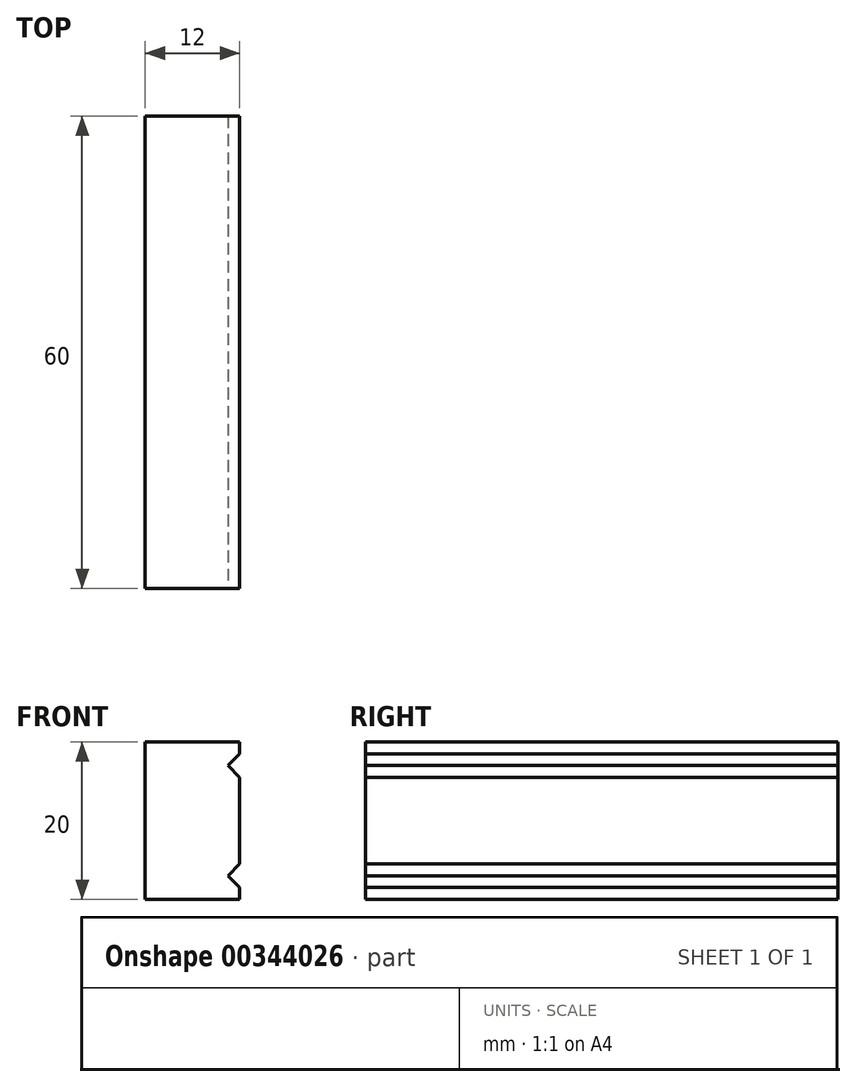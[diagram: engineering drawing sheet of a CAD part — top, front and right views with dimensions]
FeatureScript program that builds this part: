
annotation { "Feature Type Name" : "Feature", "Feature Type Description" : "" }
export const myFeature = defineFeature(function(context is Context, id is Id, definition is map)
    precondition{}
    {
        {
            var Q0;
            Q0=qCreatedBy(makeId("Right.planeOp"),FACE);
            var sketch = newSketch(context, id + "F0", { "sketchPlane" : qUnion([Q0])});
            skLineSegment(sketch, "E0.bottom", {"start": v(30, -10) * mm, "end": v(-30, -10) * mm});
            skLineSegment(sketch, "E0.top", {"start": v(30, 10) * mm, "end": v(-30, 10) * mm});
            skLineSegment(sketch, "E0.left", {"start": v(30, -10) * mm, "end": v(30, 10) * mm});
            skLineSegment(sketch, "E0.right", {"start": v(-30, -10) * mm, "end": v(-30, 10) * mm});
            skPoint(sketch, "E0.middle", {"position": v(0, 0) * mm});
            skSolve(sketch);
        }
        {
            var Q0;
            Q0=makeQuery(id+"F0.imprint","IMPRINT",FACE,{"disambiguationData":[TD([[makeQuery(id+"F0.imprint","IMPRINT",EDGE,{"derivedFrom":sQuery(id+"F0.wireOp",EDGE,"E0.bottom")}),-1.0]])]});
            extrude(context, id + "F1", {"entities" : qUnion([Q0]), "depth" : 12 * mm});
        }
        {
            var Q0;
            Q0=makeQuery(id+"F1.opExtrude","SWEPT_FACE",FACE,{"disambiguationData":[OSD([sQuery(id+"F0.wireOp",EDGE,"E0.right")])]});
            var sketch = newSketch(context, id + "F2", { "sketchPlane" : qUnion([Q0])});
            skLineSegment(sketch, "E1", {"start": v(10.5, 7) * mm, "end": v(12.79, 9.29) * mm});
            skLineSegment(sketch, "E2", {"start": v(10.5, 7) * mm, "end": v(13.4, 4.1) * mm});
            skLineSegment(sketch, "E3", {"start": v(10.5, -7) * mm, "end": v(13.13, -4.37) * mm});
            skLineSegment(sketch, "E4", {"start": v(10.5, -7) * mm, "end": v(16.17, -12.67) * mm});
            skSolve(sketch);
        }
        {
            var Q0;
            {var subQ0=sQuery(id+"F2.wireOp",EDGE,"E2");var subQ1=sQuery(id+"F2.wireOp",EDGE,"E1");var subQ2=makeQuery(id+"F2.imprint","INTERSECT",VERTEX,{"derivedFrom":[subQ1,subQ0]});Q0=makeQuery(id+"F2.imprint","IMPRINT",FACE,{"disambiguationData":[TD([[makeQuery(id+"F2.imprint","IMPRINT",EDGE,{"disambiguationData":[TD([[subQ2,-1.0]])],"derivedFrom":subQ1}),-1.0]])]});}
            var Q1;
            {var subQ0=sQuery(id+"F2.wireOp",EDGE,"E4");var subQ1=sQuery(id+"F2.wireOp",EDGE,"E3");var subQ2=makeQuery(id+"F2.imprint","INTERSECT",VERTEX,{"derivedFrom":[subQ1,subQ0]});Q1=makeQuery(id+"F2.imprint","IMPRINT",FACE,{"disambiguationData":[TD([[makeQuery(id+"F2.imprint","IMPRINT",EDGE,{"disambiguationData":[TD([[subQ2,-1.0]])],"derivedFrom":subQ1}),-1.0]])]});}
            extrude(context, id + "F3", {"entities" : qUnion([Q0, Q1]), "operationType" : NewBodyOperationType.REMOVE, "endBound" : BoundingType.THROUGH_ALL, "oppositeDirection" : true, "depth" : 25 * mm});
        }
    });
